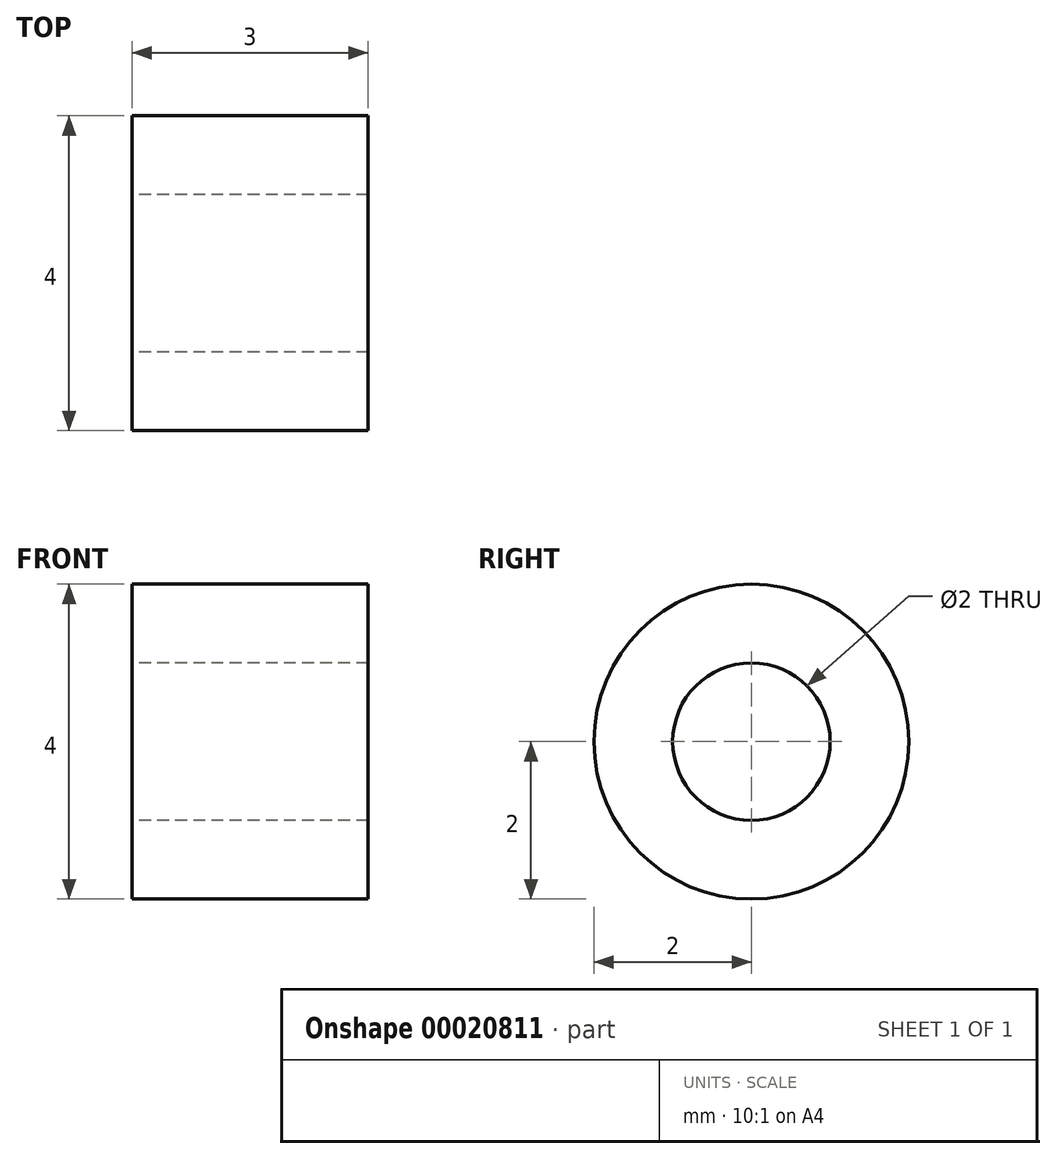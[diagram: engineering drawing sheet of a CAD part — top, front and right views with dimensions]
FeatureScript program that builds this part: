
annotation { "Feature Type Name" : "Feature", "Feature Type Description" : "" }
export const myFeature = defineFeature(function(context is Context, id is Id, definition is map)
    precondition{}
    {
        {
            var Q0;
            Q0=qCreatedBy(makeId("Right.planeOp"),FACE);
            var sketch = newSketch(context, id + "F0", { "sketchPlane" : qUnion([Q0])});
            skCircle(sketch, "E0", {"center": v(0, 0) * mm, "radius": 2 * mm});
            skCircle(sketch, "E1", {"center": v(0, 0) * mm, "radius": 1 * mm});
            skSolve(sketch);
        }
        {
            var Q0;
            Q0=makeQuery(id+"F0.imprint","IMPRINT",FACE,{"disambiguationData":[TD([[makeQuery(id+"F0.imprint","IMPRINT",EDGE,{"derivedFrom":sQuery(id+"F0.wireOp",EDGE,"E0")}),1.0]])]});
            extrude(context, id + "F1", {"entities" : qUnion([Q0]), "depth" : 3 * mm});
        }
    });
